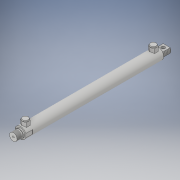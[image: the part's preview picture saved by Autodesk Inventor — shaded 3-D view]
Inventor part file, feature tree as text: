
AUTODESK INVENTOR PART (.ipt)
format: ipt  version: 2018 (Build 220112000, 112)  size: 202,240 bytes
history: native  units: in
note: dims shown in document units (in); Inventor stores cm internally (conversion verified against a paired STEP export)
features: extrude x10, sketch x10, projected_geometry x3, thread x2, plane x1
ambient origin geometry x8: Origin, YZ Plane, XZ Plane, XY Plane, X Axis, Y Axis, Z Axis, Center Point
bodies: Solid1 (feature_tree)
feature tree (26):
  extrude  "Extrusion1"  Depth=10.0in TaperAngle=0.0deg
  plane  "Work Plane1"
  extrude  "Extrusion2"  Depth=0.45in
  extrude  "Extrusion3"  Depth=0.35in
  extrude  "Extrusion5"  Depth=0.405in
  sketch  "Sketch7"  dims[d11=0.4in d12=0.4in]
  thread  "Thread1"  [1 undecoded]
  extrude  "Extrusion7"  Depth=0.4in
  extrude  "Extrusion8"  Depth=0.225in
  extrude  "Extrusion9"  Depth=0.26in
  extrude  "Extrusion10"  Depth=0.625in
  extrude  "Extrusion11"  Depth=0.01in TaperAngle=0.0deg
  thread  "Thread2"  [1 undecoded]
  extrude  "Extrusion12"  Depth=7.4in
  sketch  "Sketch1"  dims[d0=0.81in d1=10.0in d2=0.0in]
  sketch  "Sketch2"  dims[d3=0.45in d4=0.45in]
  sketch  "Sketch3"  dims[d5=0.35in d6=0.35in]
  projected_geometry  "Projected Loop1"
  projected_geometry  "Projected Loop2"
  sketch  "Sketch6"  dims[d7=0.405in d8=0.405in d9=0.5in d10=0.0in]
  projected_geometry  "Projected Loop3"
  sketch  "Sketch8"  dims[d13=0.225in d14=0.225in]
  sketch  "Sketch9"  dims[d15=0.26in d16=0.26in]
  sketch  "Sketch10"  dims[d17=0.0835in d18=0.0in d33=0.625in]
  sketch  "Sketch11"  dims[d34=0.01in d35=0.0in d40=1.0in d41=0.0in d42=0.0in]
  sketch  "Sketch12"  dims[d44=0.35in d45=0.175in d46=0.615in d47=0.0in d48=0.25in d49=0.259in d50=0.25in d51=0.615in d52=0.0in d53=0.625in d54=0.1in d55=0.0in d58=0.76in d59=0.38in d60=0.5in d61=0.0in d62=0.55in d63=0.425in d64=0.0in d65=1.0in d66=0.075in d67=0.125in d68=7.4in d69=0.0in]
note: 2 required parameter values undecoded (feature->parameter linkage not recoverable at this tier; creation-order binding heuristic only, values carry confidence <= 0.55)
